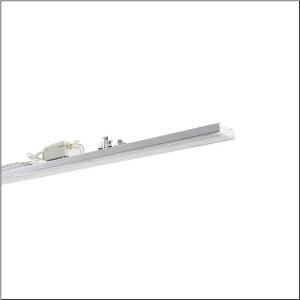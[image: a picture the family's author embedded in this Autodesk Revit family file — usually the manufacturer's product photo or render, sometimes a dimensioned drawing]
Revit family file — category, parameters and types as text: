
# Revit family: licross_r__21_recessed_ho_52te1edv4lxs_3477
name_source: partatom
category: Lighting Fixtures
units: mm (PartAtom-declared; Revit-internal decimal feet)

## family parameters
Cut with Voids When Loaded = No
Host = Face
Light Source = No
Part Type = Normal
Room Calculation Point = No
Round Connector Dimension = Use Diameter
Shared = No

## types (1)
- --- (1 x LED, 20000 lm, 112.9 W, 4000K)
    Apparent Load = 113 VA
    CIE Flux Codes = 85 95 99 100 100
    Color Rendering = 80
    Color Temperature = 4000K
    Default Elevation = 1800 mm
    Description = Licross® 21 Recessed HO, luminaire insert, of sheet steel, galvanised, coil coated, white, length: 2.250mm, width: 66mm, height: 67mm, LED rated luminous flux: 20.000lm, light colour: 840, control gear: DALI 2, with plug, 5-pole, with phase selection, mains connection: 220..240V, AC, 50/60Hz, rated input power: 113W, halogen-free wiring, primary light control with lens, of plastic, primary optical cover: cover, of PMMA, light emission: direct distribution, primary light characteristic: symmetric, protection rating (complete): IP54, insulation class (complete): insulation class I (protective earthing), certification: CE, ENEC, VDE, UKCA, protection symbol: D if used in an environment with non-conductive dust loads with corresponding accessories, impact resistance: IK06, permissible ambient temperature for indoor applications: -40..+35°C, corresponds to IFS (International Featured Standards) requirements for safety and quality in the food industry, reducing of maximum allowable ambient temperature of 5°C with ceiling mounting, LABS conformity tested according to VDMA 24364:2018-05, packaging unit: 1 piece
    Height = 58 mm
    Lamp = 1 x LED
    Lamp Light Flux = 20000 lm
    Lamp Power = 112.9 W
    Lamp count = 1
    Length = 2250 mm
    Luminous efficacy = 177 lm/W
    Manufacturer = Siteco
    ModVariant = No
    Model = 52TE1EDV4LXS
    Mounting Place = Ceiling
    Mounting Type = Pendant
    Number of Poles = 1
    OnlyDefault = Yes
    Power Factor = 1
    Product Name = Licross® 21 Recessed HO
    Product group = luminaire insert
    ProductGroupID = 901
    Protection Class = Protection class I
    Protection Degree = IP 54
    RLX_Detail_Level = 1
    RLX_Emergency_Light_Flux = 0 lm
    RLX_Emergency_Type = 0
    RLX_Emergency_Type_DB = No
    RlxData = <blob elided: 29917 chars, md5=6b62ce02>
    Socket = socket
    Standby Power = 0 W
    System Light Flux = 20000 lm
    System Power = 113 W
    Type Comments = factory setting: luminous flux: 100 % | dim-lin: 254 | 438 mA
    Type Image = l_1296930.jpg
    URL = http://relux.com
    VarID = @adj_056915
    Voltage = 0 V
    Weight = 0.00 kg
    Width = 66 mm

## geometry (parser evidence)
native form markers: Blend x4, Sweep x9
no freeform markers — native parametric forms only
